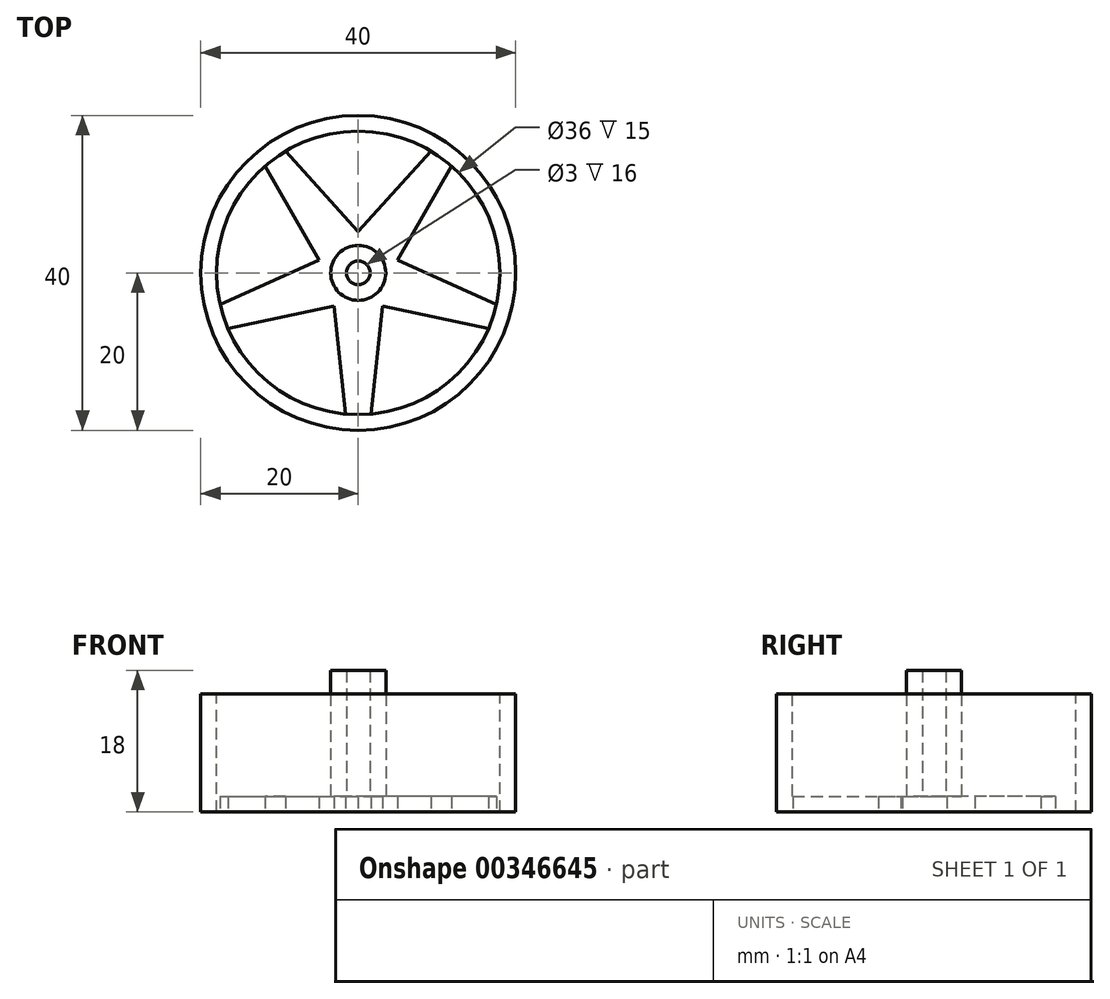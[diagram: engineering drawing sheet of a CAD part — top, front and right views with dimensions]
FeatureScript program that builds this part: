
annotation { "Feature Type Name" : "Feature", "Feature Type Description" : "" }
export const myFeature = defineFeature(function(context is Context, id is Id, definition is map)
    precondition{}
    {
        {
            var Q0;
            Q0=qCreatedBy(makeId("Top.planeOp"),FACE);
            var sketch = newSketch(context, id + "F0", { "sketchPlane" : qUnion([Q0])});
            skCircle(sketch, "E0", {"center": v(0, 0) * mm, "radius": 20 * mm});
            skSolve(sketch);
        }
        {
            var Q0;
            Q0=makeQuery(id+"F0.imprint","IMPRINT",FACE,{"disambiguationData":[TD([[makeQuery(id+"F0.imprint","IMPRINT",EDGE,{"derivedFrom":sQuery(id+"F0.wireOp",EDGE,"E0")}),1.0]])]});
            extrude(context, id + "F1", {"entities" : qUnion([Q0]), "depth" : 15 * mm});
        }
        {
            var Q0;
            Q0=makeQuery(id+"F1.opExtrude","CAP_FACE",FACE,{"disambiguationData":[OSD([sQuery(id+"F0.wireOp",EDGE,"E0")])],"isStart":false});
            var sketch = newSketch(context, id + "F2", { "sketchPlane" : qUnion([Q0])});
            skCircle(sketch, "E1", {"center": v(0, 0) * mm, "radius": 18 * mm});
            skSolve(sketch);
        }
        {
            var Q0;
            Q0=makeQuery(id+"F2.imprint","IMPRINT",FACE,{"disambiguationData":[TD([[makeQuery(id+"F2.imprint","IMPRINT",EDGE,{"derivedFrom":sQuery(id+"F2.wireOp",EDGE,"E1")}),1.0]])]});
            extrude(context, id + "F3", {"entities" : qUnion([Q0]), "operationType" : NewBodyOperationType.REMOVE, "oppositeDirection" : true, "depth" : 13 * mm});
        }
        {
            var Q0;
            Q0=makeQuery(id+"F3.boolean.opBoolean","COPY",FACE,{"derivedFrom":makeQuery(id+"F3.opExtrude","CAP_FACE",FACE,{"disambiguationData":[OSD([sQuery(id+"F2.wireOp",EDGE,"E1")])],"isStart":false})});
            var sketch = newSketch(context, id + "F4", { "sketchPlane" : qUnion([Q0])});
            skSolve(sketch);
        }
        {
            var Q0;
            Q0=makeQuery(id+"F4.imprint","IMPRINT",FACE,{"disambiguationData":[TD([[makeQuery(id+"F4.imprint","IMPRINT",EDGE,{"derivedFrom":makeQuery(id+"F3.boolean.opBoolean","COPY",EDGE,{"derivedFrom":makeQuery(id+"F3.opExtrude","CAP_EDGE",EDGE,{"disambiguationData":[OSD([sQuery(id+"F2.wireOp",EDGE,"E1")])],"isStart":false})})}),1.0]])]});
            var sketch = newSketch(context, id + "F5", { "sketchPlane" : qUnion([Q0])});
            skCircle(sketch, "E2", {"center": v(0, 0) * mm, "radius": 1.5 * mm});
            skCircle(sketch, "E3", {"center": v(0, 0) * mm, "radius": 3.5 * mm});
            skSolve(sketch);
        }
        {
            var Q0;
            Q0=makeQuery(id+"F5.imprint","IMPRINT",FACE,{"disambiguationData":[TD([[makeQuery(id+"F5.imprint","IMPRINT",EDGE,{"derivedFrom":sQuery(id+"F5.wireOp",EDGE,"E2")}),-1.0]])]});
            extrude(context, id + "F6", {"entities" : qUnion([Q0]), "operationType" : NewBodyOperationType.ADD, "depth" : 16 * mm});
        }
        {
            var Q0;
            Q0=qCreatedBy(makeId("Top.planeOp"),FACE);
            var sketch = newSketch(context, id + "F7", { "sketchPlane" : qUnion([Q0])});
            skCircle(sketch, "E4", {"center": v(0, 0) * mm, "radius": 18 * mm});
            skCircle(sketch, "E5", {"center": v(0, 0) * mm, "radius": 3.5 * mm});
            skLineSegment(sketch, "E6", {"start": v(0, -18) * mm, "end": v(1.6, -17.93) * mm});
            skLineSegment(sketch, "E7", {"start": v(1.6, -17.93) * mm, "end": v(3.07, -4.23) * mm});
            skLineSegment(sketch, "E8.MirrorCS", {"start": v(-1.6, -17.93) * mm, "end": v(-3.07, -4.23) * mm});
            skLineSegment(sketch, "E9.1.0", {"start": v(16.55, -7.07) * mm, "end": v(3.07, -4.23) * mm});
            skLineSegment(sketch, "E9.1.1", {"start": v(17.55, -4) * mm, "end": v(4.97, 1.61) * mm});
            skLineSegment(sketch, "E9.2.0", {"start": v(11.84, 13.56) * mm, "end": v(4.97, 1.61) * mm});
            skLineSegment(sketch, "E9.2.1", {"start": v(9.24, 15.45) * mm, "end": v(0, 5.22) * mm});
            skLineSegment(sketch, "E9.3.0", {"start": v(-9.24, 15.45) * mm, "end": v(0, 5.22) * mm});
            skLineSegment(sketch, "E9.3.1", {"start": v(-11.84, 13.56) * mm, "end": v(-4.97, 1.61) * mm});
            skLineSegment(sketch, "E9.4.0", {"start": v(-17.55, -4) * mm, "end": v(-4.97, 1.61) * mm});
            skLineSegment(sketch, "E9.4.1", {"start": v(-16.55, -7.07) * mm, "end": v(-3.07, -4.23) * mm});
            skLineSegment(sketch, "E10.trimOffspring", {"start": v(0, -3.58) * mm, "end": v(1.09, -3.35) * mm});
            skLineSegment(sketch, "E11.trimOffspring", {"start": v(0, -3.58) * mm, "end": v(-1.09, -3.35) * mm});
            skLineSegment(sketch, "E12.trimOffspring", {"start": v(-3.4, -1.1) * mm, "end": v(-3.52, 0) * mm});
            skLineSegment(sketch, "E13.trimOffspring", {"start": v(3.4, -1.1) * mm, "end": v(3.52, 0) * mm});
            skLineSegment(sketch, "E14.trimOffspring", {"start": v(2.1, 2.9) * mm, "end": v(1.09, 3.35) * mm});
            skLineSegment(sketch, "E15.trimOffspring", {"start": v(2.1, 2.9) * mm, "end": v(2.85, 2.07) * mm});
            skLineSegment(sketch, "E16.trimOffspring", {"start": v(-2.1, 2.9) * mm, "end": v(-2.85, 2.07) * mm});
            skLineSegment(sketch, "E17.trimOffspring", {"start": v(-2.1, 2.9) * mm, "end": v(-1.09, 3.35) * mm});
            skLineSegment(sketch, "E18.trimOffspring", {"start": v(-3.4, -1.1) * mm, "end": v(-2.85, -2.07) * mm});
            skLineSegment(sketch, "E19.trimOffspring", {"start": v(3.4, -1.1) * mm, "end": v(2.85, -2.07) * mm});
            skSolve(sketch);
        }
        {
            var Q0;
            {var subQ0=sQuery(id+"F7.wireOp",EDGE,"E8.MirrorCS");Q0=makeQuery(id+"F7.imprint","IMPRINT",FACE,{"disambiguationData":[TD([[makeQuery(id+"F7.imprint","IMPRINT",EDGE,{"derivedFrom":subQ0}),1.0]])]});}
            var Q1;
            {var subQ0=sQuery(id+"F7.wireOp",EDGE,"E7");Q1=makeQuery(id+"F7.imprint","IMPRINT",FACE,{"disambiguationData":[TD([[makeQuery(id+"F7.imprint","IMPRINT",EDGE,{"derivedFrom":subQ0}),-1.0]])]});}
            var Q2;
            {var subQ0=sQuery(id+"F7.wireOp",EDGE,"E9.1.1");Q2=makeQuery(id+"F7.imprint","IMPRINT",FACE,{"disambiguationData":[TD([[makeQuery(id+"F7.imprint","IMPRINT",EDGE,{"derivedFrom":subQ0}),-1.0]])]});}
            var Q3;
            {var subQ0=sQuery(id+"F7.wireOp",EDGE,"E9.2.1");Q3=makeQuery(id+"F7.imprint","IMPRINT",FACE,{"disambiguationData":[TD([[makeQuery(id+"F7.imprint","IMPRINT",EDGE,{"derivedFrom":subQ0}),-1.0]])]});}
            var Q4;
            {var subQ0=sQuery(id+"F7.wireOp",EDGE,"E9.3.1");Q4=makeQuery(id+"F7.imprint","IMPRINT",FACE,{"disambiguationData":[TD([[makeQuery(id+"F7.imprint","IMPRINT",EDGE,{"derivedFrom":subQ0}),-1.0]])]});}
            extrude(context, id + "F8", {"entities" : qUnion([Q0, Q1, Q2, Q3, Q4]), "operationType" : NewBodyOperationType.REMOVE, "depth" : 2 * mm});
        }
    });
